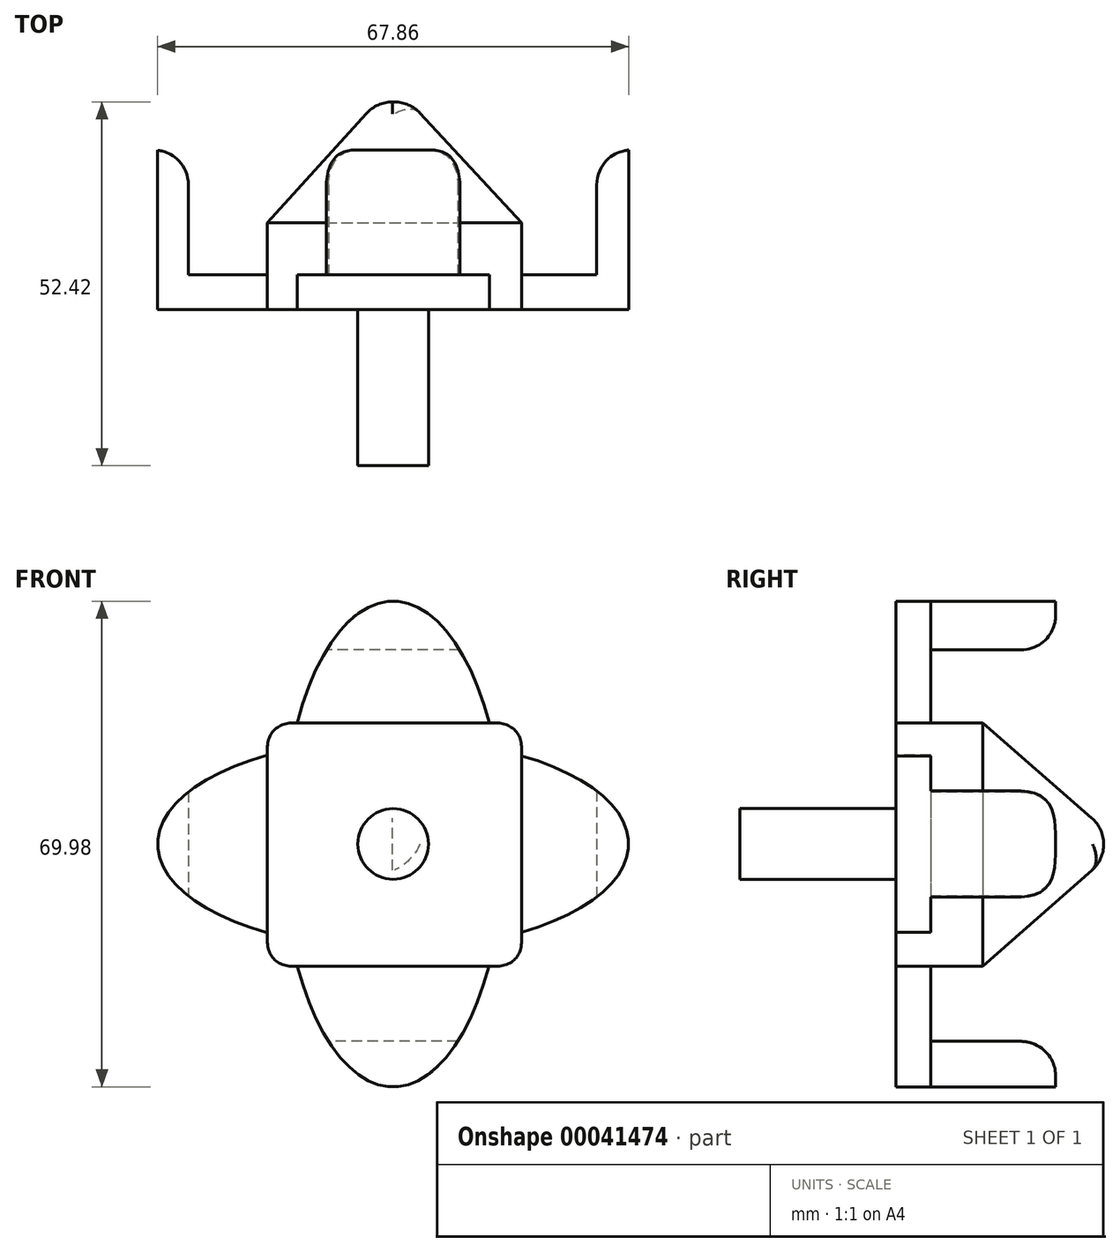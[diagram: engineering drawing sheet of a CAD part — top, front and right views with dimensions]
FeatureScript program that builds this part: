
annotation { "Feature Type Name" : "Feature", "Feature Type Description" : "" }
export const myFeature = defineFeature(function(context is Context, id is Id, definition is map)
    precondition{}
    {
        {
            var Q0;
            Q0=qCreatedBy(makeId("Front.planeOp"),FACE);
            var sketch = newSketch(context, id + "F0", { "sketchPlane" : qUnion([Q0])});
            skCircle(sketch, "E0", {"center": v(0, 0) * mm, "radius": 19.45 * mm});
            skSolve(sketch);
        }
        {
            var Q0;
            Q0=qCreatedBy(makeId("Front.planeOp"),FACE);
            cPlane(context, id + "F1", {"entities" : qUnion([Q0]), "cplaneType" : CPlaneType.OFFSET, "offset" : 20 * mm, "width" : 150 * mm, "height" : 150 * mm});
        }
        {
            var Q0;
            Q0=qCreatedBy(id+"F1.planeOp",FACE);
            var sketch = newSketch(context, id + "F2", { "sketchPlane" : qUnion([Q0])});
            skLineSegment(sketch, "E1.bottom", {"start": v(-18.12, 17.45) * mm, "end": v(18.5, 17.45) * mm});
            skLineSegment(sketch, "E1.top", {"start": v(-18.12, -17.64) * mm, "end": v(18.5, -17.64) * mm});
            skLineSegment(sketch, "E1.left", {"start": v(-18.12, 17.45) * mm, "end": v(-18.12, -17.64) * mm});
            skLineSegment(sketch, "E1.right", {"start": v(18.5, 17.45) * mm, "end": v(18.5, -17.64) * mm});
            skSolve(sketch);
        }
        {
            var Q0;
            Q0=sQuery(id+"F0.wireOp",VERTEX,"E0.center");
            var Q1;
            Q1=makeQuery(id+"F2.imprint","IMPRINT",FACE,{"disambiguationData":[TD([[makeQuery(id+"F2.imprint","IMPRINT",EDGE,{"derivedFrom":sQuery(id+"F2.wireOp",EDGE,"E1.bottom")}),-1.0]])]});
            loft(context, id + "F3", {"sheetProfilesArray" : [{ "sheetProfileEntities" : qUnion([Q0]) }, { "sheetProfileEntities" : qUnion([Q1]) }]});
        }
        {
            var Q0;
            Q0=makeQuery(id+"F3.opLoft","SWEPT_EDGE",EDGE,{"disambiguationData":[OSD([sQuery(id+"F0.wireOp",VERTEX,"E0.center"),sQuery(id+"F2.wireOp",EDGE,"E1.top"),sQuery(id+"F2.wireOp",EDGE,"E1.right")])]});
            fillet(context, id + "F4", {"entities" : qUnion([Q0]), "radius" : 5 * mm, "tangentPropagation" : true, "allowEdgeOverflow" : false});
        }
        {
            var Q0;
            Q0=makeQuery(id+"F3.opLoft","SWEPT_EDGE",EDGE,{"disambiguationData":[OSD([sQuery(id+"F0.wireOp",VERTEX,"E0.center"),sQuery(id+"F2.wireOp",EDGE,"E1.bottom"),sQuery(id+"F2.wireOp",EDGE,"E1.right")])]});
            fillet(context, id + "F5", {"entities" : qUnion([Q0]), "radius" : 5 * mm, "tangentPropagation" : true, "allowEdgeOverflow" : false});
        }
        {
            var Q0;
            Q0=makeQuery(id+"F3.opLoft","SWEPT_EDGE",EDGE,{"disambiguationData":[OSD([sQuery(id+"F0.wireOp",VERTEX,"E0.center"),sQuery(id+"F2.wireOp",EDGE,"E1.top"),sQuery(id+"F2.wireOp",EDGE,"E1.left")])]});
            fillet(context, id + "F6", {"entities" : qUnion([Q0]), "radius" : 5 * mm, "tangentPropagation" : true, "allowEdgeOverflow" : false});
        }
        {
            var Q0;
            Q0=makeQuery(id+"F3.opLoft","CAP_FACE",FACE,{"disambiguationData":[OSD([makeQuery(id+"F2.imprint","IMPRINT",FACE,{"disambiguationData":[TD([[makeQuery(id+"F2.imprint","IMPRINT",EDGE,{"derivedFrom":sQuery(id+"F2.wireOp",EDGE,"E1.bottom")}),-1.0]])]})])],"isStart":true});
            extrude(context, id + "F7", {"entities" : qUnion([Q0]), "operationType" : NewBodyOperationType.ADD, "depth" : 5 * mm});
        }
        {
            var Q0;
            Q0=makeQuery(id+"F7.opExtrude","CAP_FACE",FACE,{"disambiguationData":[OSD([makeQuery(id+"F2.imprint","IMPRINT",FACE,{"disambiguationData":[TD([[makeQuery(id+"F2.imprint","IMPRINT",EDGE,{"derivedFrom":sQuery(id+"F2.wireOp",EDGE,"E1.bottom")}),-1.0]])]})])],"isStart":false});
            var sketch = newSketch(context, id + "F8", { "sketchPlane" : qUnion([Q0])});
            skCircle(sketch, "E2", {"center": v(0, 0) * mm, "radius": 5.09 * mm});
            skSolve(sketch);
        }
        {
            var Q0;
            Q0=makeQuery(id+"F8.imprint","IMPRINT",FACE,{"disambiguationData":[TD([[makeQuery(id+"F8.imprint","IMPRINT",EDGE,{"derivedFrom":sQuery(id+"F8.wireOp",EDGE,"E2")}),1.0]])]});
            extrude(context, id + "F9", {"entities" : qUnion([Q0]), "operationType" : NewBodyOperationType.ADD, "depth" : 30 * mm});
        }
        {
            var Q0;
            Q0=makeQuery(id+"F7.opExtrude","CAP_FACE",FACE,{"disambiguationData":[OSD([makeQuery(id+"F2.imprint","IMPRINT",FACE,{"disambiguationData":[TD([[makeQuery(id+"F2.imprint","IMPRINT",EDGE,{"derivedFrom":sQuery(id+"F2.wireOp",EDGE,"E1.bottom")}),-1.0]])]})])],"isStart":false});
            extrude(context, id + "F10", {"entities" : qUnion([Q0]), "operationType" : NewBodyOperationType.ADD, "depth" : 5 * mm});
        }
        {
            var Q0;
            Q0=makeQuery(id+"F10.opExtrude","CAP_FACE",FACE,{"disambiguationData":[OSD([makeQuery(id+"F2.imprint","IMPRINT",FACE,{"disambiguationData":[TD([[makeQuery(id+"F2.imprint","IMPRINT",EDGE,{"derivedFrom":sQuery(id+"F2.wireOp",EDGE,"E1.bottom")}),-1.0]])]})])],"isStart":false});
            extrude(context, id + "F11", {"entities" : qUnion([Q0]), "operationType" : NewBodyOperationType.ADD, "depth" : 2.5 * mm});
        }
        {
            var Q0;
            Q0=makeQuery(id+"F11.opExtrude","CAP_FACE",FACE,{"disambiguationData":[OSD([makeQuery(id+"F2.imprint","IMPRINT",FACE,{"disambiguationData":[TD([[makeQuery(id+"F2.imprint","IMPRINT",EDGE,{"derivedFrom":sQuery(id+"F2.wireOp",EDGE,"E1.bottom")}),-1.0]])]})])],"isStart":false});
            var sketch = newSketch(context, id + "F12", { "sketchPlane" : qUnion([Q0])});
            skEllipse(sketch, "E3", {"center": v(0, 0) * mm, "majorRadius": 34.99 * mm, "minorRadius": 15.97 * mm, "majorAxis": v(0, 1)});
            skEllipse(sketch, "E4", {"center": v(0, 0) * mm, "majorRadius": 33.93 * mm, "minorRadius": 15.16 * mm, "majorAxis": v(-1, 0)});
            skSolve(sketch);
        }
        {
            var Q0;
            {var subQ0=makeQuery(id+"F11.opExtrude","CAP_EDGE",EDGE,{"disambiguationData":[OSD([sQuery(id+"F2.wireOp",EDGE,"E1.bottom"),sQuery(id+"F2.wireOp",EDGE,"E1.left"),sQuery(id+"F2.wireOp",EDGE,"E1.right")])],"isStart":false});var subQ1=sQuery(id+"F12.wireOp",EDGE,"E3");var subQ3=makeQuery(id+"F12.imprint","INTERSECT",VERTEX,{"disambiguationData":[OD(0.0)],"derivedFrom":[subQ0,subQ1]});Q0=makeQuery(id+"F12.imprint","IMPRINT",FACE,{"disambiguationData":[TD([[makeQuery(id+"F12.imprint","IMPRINT",EDGE,{"disambiguationData":[TD([[subQ3,1.0]])],"derivedFrom":subQ1}),1.0]])]});}
            var Q1;
            {var subQ0=makeQuery(id+"F11.opExtrude","CAP_EDGE",EDGE,{"disambiguationData":[OSD([sQuery(id+"F2.wireOp",EDGE,"E1.bottom"),sQuery(id+"F2.wireOp",EDGE,"E1.top"),sQuery(id+"F2.wireOp",EDGE,"E1.left")])],"isStart":false});var subQ1=sQuery(id+"F12.wireOp",EDGE,"E4");var subQ3=makeQuery(id+"F12.imprint","INTERSECT",VERTEX,{"disambiguationData":[OD(0.0)],"derivedFrom":[subQ0,subQ1]});Q1=makeQuery(id+"F12.imprint","IMPRINT",FACE,{"disambiguationData":[TD([[makeQuery(id+"F12.imprint","IMPRINT",EDGE,{"disambiguationData":[TD([[subQ3,1.0]])],"derivedFrom":subQ1}),1.0]])]});}
            var Q2;
            {var subQ0=makeQuery(id+"F11.opExtrude","CAP_EDGE",EDGE,{"disambiguationData":[OSD([sQuery(id+"F2.wireOp",EDGE,"E1.top"),sQuery(id+"F2.wireOp",EDGE,"E1.left"),sQuery(id+"F2.wireOp",EDGE,"E1.right")])],"isStart":false});var subQ1=sQuery(id+"F12.wireOp",EDGE,"E3");var subQ3=makeQuery(id+"F12.imprint","INTERSECT",VERTEX,{"disambiguationData":[OD(0.0)],"derivedFrom":[subQ0,subQ1]});Q2=makeQuery(id+"F12.imprint","IMPRINT",FACE,{"disambiguationData":[TD([[makeQuery(id+"F12.imprint","IMPRINT",EDGE,{"disambiguationData":[TD([[subQ3,-1.0]])],"derivedFrom":subQ1}),1.0]])]});}
            var Q3;
            {var subQ0=makeQuery(id+"F11.opExtrude","CAP_EDGE",EDGE,{"disambiguationData":[OSD([sQuery(id+"F2.wireOp",EDGE,"E1.bottom"),sQuery(id+"F2.wireOp",EDGE,"E1.top"),sQuery(id+"F2.wireOp",EDGE,"E1.right")])],"isStart":false});var subQ1=sQuery(id+"F12.wireOp",EDGE,"E4");var subQ3=makeQuery(id+"F12.imprint","INTERSECT",VERTEX,{"disambiguationData":[OD(0.0)],"derivedFrom":[subQ0,subQ1]});Q3=makeQuery(id+"F12.imprint","IMPRINT",FACE,{"disambiguationData":[TD([[makeQuery(id+"F12.imprint","IMPRINT",EDGE,{"disambiguationData":[TD([[subQ3,-1.0]])],"derivedFrom":subQ1}),1.0]])]});}
            extrude(context, id + "F13", {"entities" : qUnion([Q0, Q1, Q2, Q3]), "oppositeDirection" : true, "depth" : 5 * mm});
        }
        {
            var Q0;
            Q0=makeQuery(id+"F13.opExtrude","CAP_FACE",FACE,{"disambiguationData":[OSD([sQuery(id+"F2.wireOp",EDGE,"E1.bottom"),sQuery(id+"F2.wireOp",EDGE,"E1.left"),sQuery(id+"F2.wireOp",EDGE,"E1.right"),sQuery(id+"F12.wireOp",EDGE,"E3")])],"isStart":false});
            var sketch = newSketch(context, id + "F14", { "sketchPlane" : qUnion([Q0])});
            skLineSegment(sketch, "E5", {"start": v(-9.6, 27.96) * mm, "end": v(9.6, 27.96) * mm});
            skSolve(sketch);
        }
        {
            var Q0;
            Q0=makeQuery(id+"F13.opExtrude","CAP_FACE",FACE,{"disambiguationData":[OSD([sQuery(id+"F2.wireOp",EDGE,"E1.top"),sQuery(id+"F2.wireOp",EDGE,"E1.left"),sQuery(id+"F2.wireOp",EDGE,"E1.right"),sQuery(id+"F12.wireOp",EDGE,"E3")])],"isStart":false});
            var sketch = newSketch(context, id + "F15", { "sketchPlane" : qUnion([Q0])});
            skLineSegment(sketch, "E6", {"start": v(-9.3, -28.44) * mm, "end": v(9.3, -28.44) * mm});
            skLineSegment(sketch, "E7", {"start": v(-28.73, 8.25) * mm, "end": v(-28.73, -7.47) * mm});
            skLineSegment(sketch, "E8", {"start": v(28.16, 8.35) * mm, "end": v(28.16, -7.88) * mm});
            skSolve(sketch);
        }
        {
            var Q0;
            {var subQ3=sQuery(id+"F14.wireOp",EDGE,"E5");Q0=makeQuery(id+"F14.imprint","IMPRINT",FACE,{"disambiguationData":[TD([[makeQuery(id+"F14.imprint","IMPRINT",EDGE,{"derivedFrom":subQ3}),1.0]])]});}
            var Q1;
            {var subQ3=sQuery(id+"F15.wireOp",EDGE,"E6");Q1=makeQuery(id+"F15.imprint","IMPRINT",FACE,{"disambiguationData":[TD([[makeQuery(id+"F15.imprint","IMPRINT",EDGE,{"derivedFrom":subQ3}),-1.0]])]});}
            extrude(context, id + "F16", {"entities" : qUnion([Q0, Q1]), "depth" : 18 * mm});
        }
        {
            var Q0;
            Q0=makeQuery(id+"F13.opExtrude","CAP_FACE",FACE,{"disambiguationData":[OSD([sQuery(id+"F2.wireOp",EDGE,"E1.bottom"),sQuery(id+"F2.wireOp",EDGE,"E1.top"),sQuery(id+"F2.wireOp",EDGE,"E1.right"),sQuery(id+"F12.wireOp",EDGE,"E4")])],"isStart":false});
            var sketch = newSketch(context, id + "F17", { "sketchPlane" : qUnion([Q0])});
            skLineSegment(sketch, "E9", {"start": v(-29.32, 7.63) * mm, "end": v(-29.32, -7.63) * mm});
            skLineSegment(sketch, "E10", {"start": v(29.49, 7.63) * mm, "end": v(29.49, -7.63) * mm});
            skSolve(sketch);
        }
        {
            var Q0;
            {var subQ3=sQuery(id+"F17.wireOp",EDGE,"E9");Q0=makeQuery(id+"F17.imprint","IMPRINT",FACE,{"disambiguationData":[TD([[makeQuery(id+"F17.imprint","IMPRINT",EDGE,{"derivedFrom":subQ3}),-1.0]])]});}
            extrude(context, id + "F18", {"entities" : qUnion([Q0]), "operationType" : NewBodyOperationType.ADD, "depth" : 18 * mm});
        }
        {
            var Q0;
            Q0=makeQuery(id+"F13.opExtrude","CAP_FACE",FACE,{"disambiguationData":[OSD([sQuery(id+"F2.wireOp",EDGE,"E1.bottom"),sQuery(id+"F2.wireOp",EDGE,"E1.top"),sQuery(id+"F2.wireOp",EDGE,"E1.left"),sQuery(id+"F12.wireOp",EDGE,"E4")])],"isStart":false});
            var sketch = newSketch(context, id + "F19", { "sketchPlane" : qUnion([Q0])});
            skLineSegment(sketch, "E11", {"start": v(29.49, 7.5) * mm, "end": v(29.49, -7.5) * mm});
            skSolve(sketch);
        }
        {
            var Q0;
            {var subQ3=sQuery(id+"F19.wireOp",EDGE,"E11");Q0=makeQuery(id+"F19.imprint","IMPRINT",FACE,{"disambiguationData":[TD([[makeQuery(id+"F19.imprint","IMPRINT",EDGE,{"derivedFrom":subQ3}),1.0]])]});}
            extrude(context, id + "F20", {"entities" : qUnion([Q0]), "operationType" : NewBodyOperationType.ADD, "depth" : 18 * mm});
        }
        {
            var Q0;
            Q0=makeQuery(id+"F20.opExtrude","CAP_EDGE",EDGE,{"disambiguationData":[OSD([sQuery(id+"F19.wireOp",EDGE,"E11")])],"isStart":false});
            fillet(context, id + "F21", {"entities" : qUnion([Q0]), "radius" : 5 * mm, "tangentPropagation" : true, "allowEdgeOverflow" : false});
        }
        {
            var Q0;
            Q0=makeQuery(id+"F16.opExtrude","CAP_EDGE",EDGE,{"disambiguationData":[OSD([sQuery(id+"F14.wireOp",EDGE,"E5")])],"isStart":false});
            fillet(context, id + "F22", {"entities" : qUnion([Q0]), "radius" : 5 * mm, "tangentPropagation" : true, "allowEdgeOverflow" : false});
        }
        {
            var Q0;
            Q0=makeQuery(id+"F18.opExtrude","CAP_EDGE",EDGE,{"disambiguationData":[OSD([sQuery(id+"F17.wireOp",EDGE,"E9")])],"isStart":false});
            fillet(context, id + "F23", {"entities" : qUnion([Q0]), "radius" : 5 * mm, "tangentPropagation" : true, "allowEdgeOverflow" : false});
        }
        {
            var Q0;
            Q0=makeQuery(id+"F16.opExtrude","CAP_EDGE",EDGE,{"disambiguationData":[OSD([sQuery(id+"F15.wireOp",EDGE,"E6")])],"isStart":false});
            fillet(context, id + "F24", {"entities" : qUnion([Q0]), "radius" : 5 * mm, "tangentPropagation" : true, "allowEdgeOverflow" : false});
        }
    });
